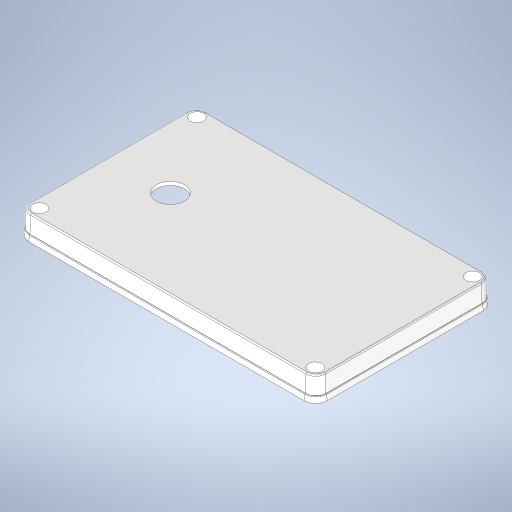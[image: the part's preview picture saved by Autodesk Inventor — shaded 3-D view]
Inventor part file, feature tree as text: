
AUTODESK INVENTOR PART (.ipt)
format: ipt  version: 2024.2 (Build 282272000, 272)  size: 358,400 bytes
history: native  units: in
note: dims shown in document units (in); Inventor stores cm internally (conversion verified against a paired STEP export)
features: extrude x1, sketch x1, other x1
ambient origin geometry x8: Origin, YZ Plane, XZ Plane, XY Plane, X Axis, Y Axis, Z Axis, Center Point
bodies: Solid1 (feature_tree)
feature tree (3):
  extrude  "Extrusion1"  Depth=0.3937in
  sketch  "Sketch1"  dims[d0=2.0669in d1=0.9449in d2=0.3937in d3=0.0in]
  other  "TOP OF LID"
